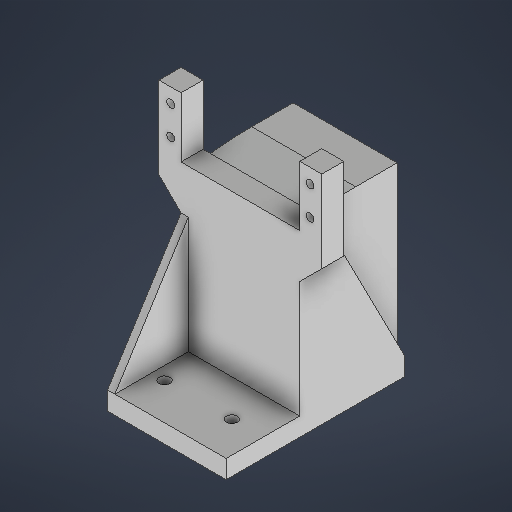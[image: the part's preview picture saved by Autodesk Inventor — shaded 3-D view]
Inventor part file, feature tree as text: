
AUTODESK INVENTOR PART (.ipt)
format: ipt  version: 2025.2 (Build 292293000, 293)  size: 286,208 bytes
history: native  units: in
note: dims shown in document units (in); Inventor stores cm internally (conversion verified against a paired STEP export)
features: extrude x7, sketch x6, fillet x1
ambient origin geometry x8: Origin, YZ Plane, XZ Plane, XY Plane, X Axis, Y Axis, Z Axis, Center Point
bodies: Solid1 (feature_tree)
feature tree (14):
  extrude  "Extrusion1"  Depth=0.3in
  extrude  "Extrusion2"  Depth=0.3in
  extrude  "Extrusion3"  Depth=0.3in
  sketch  "Sketch4"  dims[d33=0.14in d34=0.1065in]
  extrude  "Extrusion6"  Depth=0.1065in
  extrude  "Extrusion7"  Depth=0.1969in
  extrude  "Extrusion8"  Depth=4.55in
  extrude  "Extrusion11"  Depth=4.55in
  fillet  "Fillet1"  Radius=0.14in
  sketch  "Sketch1"  dims[d24=2.215in d28=0.3in]
  sketch  "Sketch2"  dims[d29=0.3in d30=1.115in]
  sketch  "Sketch3"  dims[d31=0.3in d32=0.1065in]
  sketch  "Sketch7"  dims[d35=0.14in d36=0.1969in]
  sketch  "Sketch10"  dims[d37=0.5906in d38=0.1065in d39=0.1065in d40=0.14in d41=0.14in d42=0.5906in d43=0.1969in d44=1.615in d52=2.1352in d53=45.0deg d54=135.0deg d55=0.3in d56=0.0in d65=1.3in d66=1.615in d67=0.15in d68=0.15in d69=0.5in d70=0.5in d71=0.275in d72=0.425in d73=0.25in d74=0.0in d75=0.1in d76=0.0in d99=0.25in d102=1.125in d103=2.485in d104=0.1in d105=0.0in d106=1.615in d107=0.0in d111=2.185in d112=1.125in d113=90.0deg d114=0.1in d115=0.0in d121=2.22in d122=0.0in d123=4.55in]
